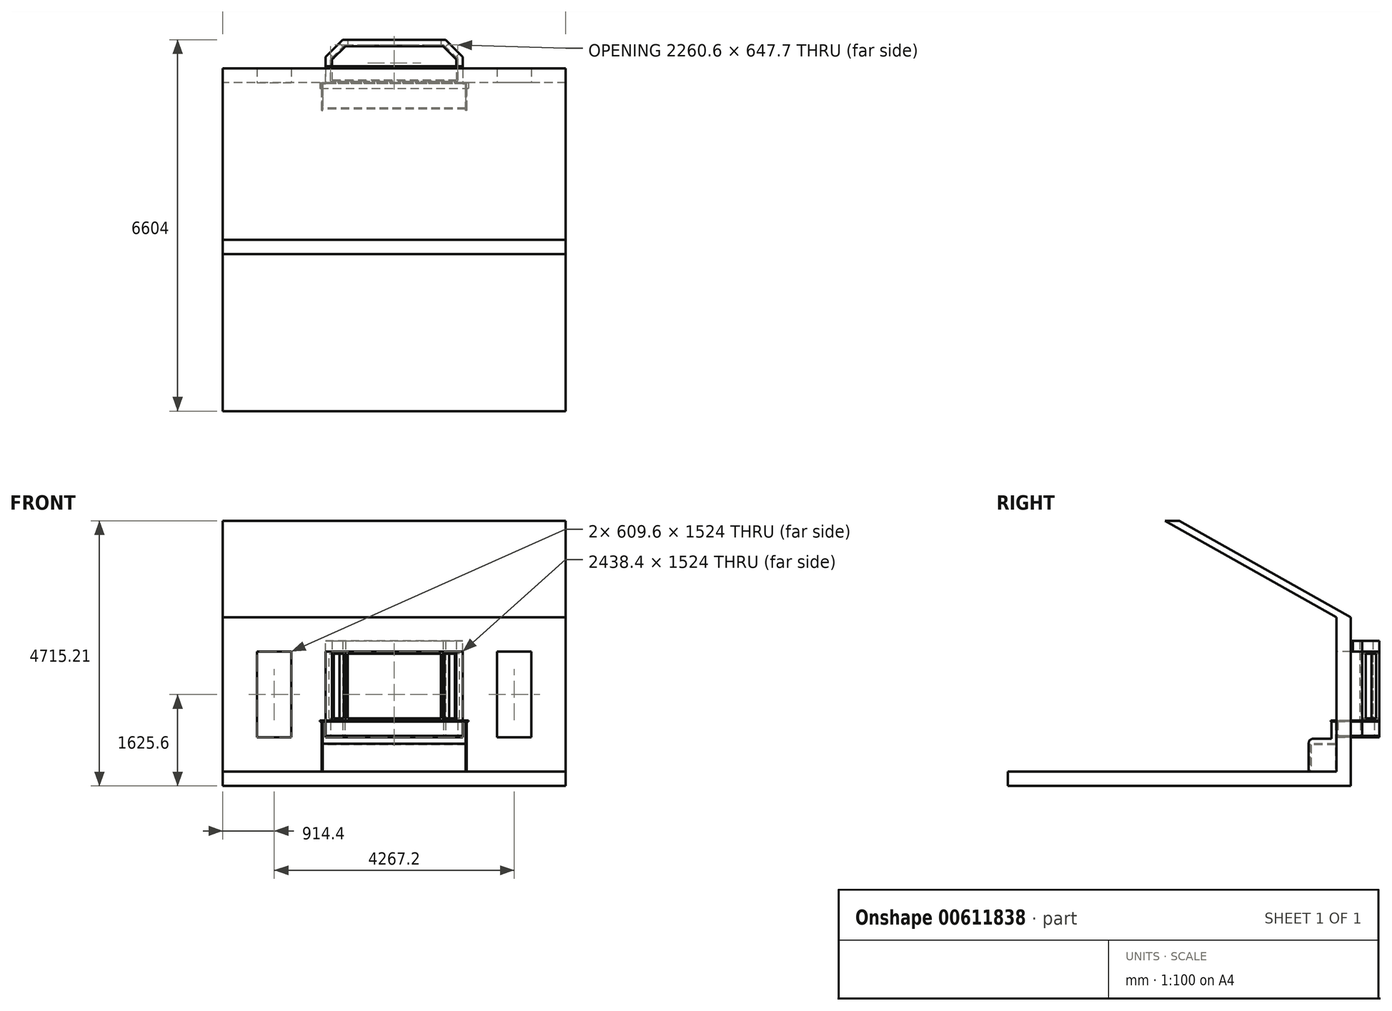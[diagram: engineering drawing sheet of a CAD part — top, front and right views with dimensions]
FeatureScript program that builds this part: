
annotation { "Feature Type Name" : "Feature", "Feature Type Description" : "" }
export const myFeature = defineFeature(function(context is Context, id is Id, definition is map)
    precondition{}
    {
        {
            var Q0;
            Q0=qCreatedBy(makeId("Top.planeOp"),FACE);
            var sketch = newSketch(context, id + "F0", { "sketchPlane" : qUnion([Q0])});
            skLineSegment(sketch, "E0.bottom", {"start": v(-3048, -3048) * mm, "end": v(3048, -3048) * mm});
            skLineSegment(sketch, "E0.top", {"start": v(-3048, 3048) * mm, "end": v(3048, 3048) * mm});
            skLineSegment(sketch, "E0.left", {"start": v(-3048, -3048) * mm, "end": v(-3048, 3048) * mm});
            skLineSegment(sketch, "E0.right", {"start": v(3048, -3048) * mm, "end": v(3048, 3048) * mm});
            skPoint(sketch, "E0.middle", {"position": v(0, 0) * mm});
            skSolve(sketch);
        }
        {
            var Q0;
            Q0=makeQuery(id+"F0.imprint","IMPRINT",FACE,{"disambiguationData":[TD([[makeQuery(id+"F0.imprint","IMPRINT",EDGE,{"derivedFrom":sQuery(id+"F0.wireOp",EDGE,"E0.bottom")}),1.0]])]});
            extrude(context, id + "F1", {"entities" : qUnion([Q0]), "oppositeDirection" : true, "depth" : 254 * mm, "offsetDistance" : 25.4 * mm});
        }
        {
            var Q0;
            Q0=makeQuery(id+"F1.opExtrude","CAP_FACE",FACE,{"disambiguationData":[OSD([sQuery(id+"F0.wireOp",EDGE,"E0.bottom"),sQuery(id+"F0.wireOp",EDGE,"E0.top"),sQuery(id+"F0.wireOp",EDGE,"E0.left"),sQuery(id+"F0.wireOp",EDGE,"E0.right")])],"isStart":true});
            var sketch = newSketch(context, id + "F2", { "sketchPlane" : qUnion([Q0])});
            skLineSegment(sketch, "E1.bottom", {"start": v(3048, 3048) * mm, "end": v(-3048, 3048) * mm});
            skLineSegment(sketch, "E1.top", {"start": v(3048, 2794) * mm, "end": v(-3048, 2794) * mm});
            skLineSegment(sketch, "E1.left", {"start": v(3048, 3048) * mm, "end": v(3048, 2794) * mm});
            skLineSegment(sketch, "E1.right", {"start": v(-3048, 3048) * mm, "end": v(-3048, 2794) * mm});
            skSolve(sketch);
        }
        {
            var Q0;
            Q0=makeQuery(id+"F2.imprint","IMPRINT",FACE,{"disambiguationData":[TD([[makeQuery(id+"F2.imprint","IMPRINT",EDGE,{"derivedFrom":sQuery(id+"F2.wireOp",EDGE,"E1.bottom")}),-1.0]])]});
            extrude(context, id + "F3", {"entities" : qUnion([Q0]), "operationType" : NewBodyOperationType.ADD, "depth" : 2743.2 * mm, "offsetDistance" : 25.4 * mm});
        }
        {
            var Q0;
            Q0=makeQuery(id+"F3.boolean.opBoolean","MERGE",FACE,{"derivedFrom":[makeQuery(id+"F1.opExtrude","SWEPT_FACE",FACE,{"disambiguationData":[OSD([sQuery(id+"F0.wireOp",EDGE,"E0.right")])]}),makeQuery(id+"F3.opExtrude","SWEPT_FACE",FACE,{"disambiguationData":[OSD([sQuery(id+"F2.wireOp",EDGE,"E1.left")])]})]});
            var sketch = newSketch(context, id + "F4", { "sketchPlane" : qUnion([Q0])});
            skLineSegment(sketch, "E2", {"start": v(3048, 2743.2) * mm, "end": v(0, 4461.21) * mm});
            skLineSegment(sketch, "E3", {"start": v(0, 4461.21) * mm, "end": v(-254, 4461.21) * mm});
            skLineSegment(sketch, "E4", {"start": v(-254, 4461.21) * mm, "end": v(2794, 2743.2) * mm});
            skLineSegment(sketch, "E5", {"start": v(2794, 2743.2) * mm, "end": v(3048, 2743.2) * mm});
            skSolve(sketch);
        }
        {
            var Q0;
            Q0=makeQuery(id+"F4.imprint","IMPRINT",FACE,{"disambiguationData":[TD([[makeQuery(id+"F4.imprint","IMPRINT",EDGE,{"derivedFrom":sQuery(id+"F4.wireOp",EDGE,"E2")}),1.0]])]});
            extrude(context, id + "F5", {"entities" : qUnion([Q0]), "operationType" : NewBodyOperationType.ADD, "oppositeDirection" : true, "depth" : 6096 * mm, "offsetDistance" : 25.4 * mm});
        }
        {
            var Q0;
            Q0=makeQuery(id+"F3.opExtrude","SWEPT_FACE",FACE,{"disambiguationData":[OSD([sQuery(id+"F2.wireOp",EDGE,"E1.top")])]});
            var sketch = newSketch(context, id + "F6", { "sketchPlane" : qUnion([Q0])});
            skLineSegment(sketch, "E6", {"start": v(0, 0) * mm, "end": v(0, 2743.2) * mm, "construction": true});
            skLineSegment(sketch, "E7", {"start": v(-3048, 1371.6) * mm, "end": v(3048, 1371.6) * mm, "construction": true});
            skLineSegment(sketch, "E8.bottom", {"start": v(-2438.4, 2133.6) * mm, "end": v(-1828.8, 2133.6) * mm});
            skLineSegment(sketch, "E8.top", {"start": v(-2438.4, 609.6) * mm, "end": v(-1828.8, 609.6) * mm});
            skLineSegment(sketch, "E8.left", {"start": v(-2438.4, 2133.6) * mm, "end": v(-2438.4, 609.6) * mm});
            skLineSegment(sketch, "E8.right", {"start": v(-1828.8, 2133.6) * mm, "end": v(-1828.8, 609.6) * mm});
            skPoint(sketch, "E8.middle", {"position": v(-2133.6, 1371.6) * mm});
            skLineSegment(sketch, "E9.MirrorCS", {"start": v(1828.8, 2133.6) * mm, "end": v(1828.8, 609.6) * mm});
            skLineSegment(sketch, "E10.MirrorCS", {"start": v(2438.4, 2133.6) * mm, "end": v(1828.8, 2133.6) * mm});
            skLineSegment(sketch, "E11.MirrorCS", {"start": v(2438.4, 2133.6) * mm, "end": v(2438.4, 609.6) * mm});
            skLineSegment(sketch, "E12.MirrorCS", {"start": v(2438.4, 609.6) * mm, "end": v(1828.8, 609.6) * mm});
            skSolve(sketch);
        }
        {
            var Q0;
            Q0=makeQuery(id+"F6.imprint","IMPRINT",FACE,{"disambiguationData":[TD([[makeQuery(id+"F6.imprint","IMPRINT",EDGE,{"derivedFrom":sQuery(id+"F6.wireOp",EDGE,"E8.bottom")}),-1.0]])]});
            var Q1;
            Q1=makeQuery(id+"F6.imprint","IMPRINT",FACE,{"disambiguationData":[TD([[makeQuery(id+"F6.imprint","IMPRINT",EDGE,{"derivedFrom":sQuery(id+"F6.wireOp",EDGE,"E9.MirrorCS")}),1.0]])]});
            extrude(context, id + "F7", {"entities" : qUnion([Q0, Q1]), "operationType" : NewBodyOperationType.REMOVE, "oppositeDirection" : true, "depth" : 304.8 * mm, "offsetDistance" : 25.4 * mm});
        }
        {
            var Q0;
            Q0=makeQuery(id+"F3.opExtrude","SWEPT_FACE",FACE,{"disambiguationData":[OSD([sQuery(id+"F2.wireOp",EDGE,"E1.top")])]});
            var sketch = newSketch(context, id + "F8", { "sketchPlane" : qUnion([Q0])});
            skLineSegment(sketch, "E13", {"start": v(0, 2743.2) * mm, "end": v(0, 0) * mm, "construction": true});
            skLineSegment(sketch, "E14", {"start": v(3048, 1371.6) * mm, "end": v(-3048, 1371.6) * mm, "construction": true});
            skLineSegment(sketch, "E15.bottom", {"start": v(1219.2, 2133.6) * mm, "end": v(-1219.2, 2133.6) * mm});
            skLineSegment(sketch, "E15.top", {"start": v(1219.2, 609.6) * mm, "end": v(-1219.2, 609.6) * mm});
            skLineSegment(sketch, "E15.left", {"start": v(1219.2, 2133.6) * mm, "end": v(1219.2, 609.6) * mm});
            skLineSegment(sketch, "E15.right", {"start": v(-1219.2, 2133.6) * mm, "end": v(-1219.2, 609.6) * mm});
            skPoint(sketch, "E15.middle", {"position": v(0, 1371.6) * mm});
            skSolve(sketch);
        }
        {
            var Q0;
            Q0 = qSketchRegion(id + "F8", true);
            extrude(context, id + "F9", {"entities" : qUnion([Q0]), "operationType" : NewBodyOperationType.REMOVE, "oppositeDirection" : true, "depth" : 304.8 * mm, "offsetDistance" : 25.4 * mm});
        }
        {
            var Q0;
            Q0=makeQuery(id+"F9.boolean.opBoolean","COPY",FACE,{"derivedFrom":makeQuery(id+"F9.opExtrude","SWEPT_FACE",FACE,{"disambiguationData":[OSD([sQuery(id+"F8.wireOp",EDGE,"E15.top")])]})});
            var sketch = newSketch(context, id + "F10", { "sketchPlane" : qUnion([Q0])});
            skLineSegment(sketch, "E16", {"start": v(-1219.2, 2794) * mm, "end": v(-1219.2, 3251.2) * mm});
            skLineSegment(sketch, "E17", {"start": v(-1219.2, 3251.2) * mm, "end": v(-914.4, 3556) * mm});
            skLineSegment(sketch, "E18", {"start": v(914.4, 3556) * mm, "end": v(1219.2, 3251.2) * mm});
            skLineSegment(sketch, "E19", {"start": v(1219.2, 3251.2) * mm, "end": v(1219.2, 2794) * mm});
            skLineSegment(sketch, "E20", {"start": v(1219.2, 2794) * mm, "end": v(0, 2794) * mm});
            skLineSegment(sketch, "E21", {"start": v(0, 2794) * mm, "end": v(-1219.2, 2794) * mm});
            skLineSegment(sketch, "E22", {"start": v(-914.4, 3556) * mm, "end": v(914.4, 3556) * mm});
            skSolve(sketch);
        }
        {
            var Q0;
            {var subQ1=sQuery(id+"F10.wireOp",EDGE,"E17");Q0=makeQuery(id+"F10.imprint","IMPRINT",FACE,{"disambiguationData":[TD([[makeQuery(id+"F10.imprint","IMPRINT",EDGE,{"derivedFrom":subQ1}),-1.0]])]});}
            var Q1;
            {var subQ1=sQuery(id+"F10.wireOp",EDGE,"E20");Q1=makeQuery(id+"F10.imprint","IMPRINT",FACE,{"disambiguationData":[TD([[makeQuery(id+"F10.imprint","IMPRINT",EDGE,{"derivedFrom":subQ1}),-1.0]])]});}
            extrude(context, id + "F11", {"entities" : qUnion([Q0, Q1]), "depth" : 25.4 * mm, "offsetDistance" : 25.4 * mm});
        }
        {
            var Q0;
            Q0=makeQuery(id+"F11.opExtrude","CAP_FACE",FACE,{"disambiguationData":[OSD([sQuery(id+"F10.wireOp",EDGE,"E16"),sQuery(id+"F10.wireOp",EDGE,"E17"),sQuery(id+"F10.wireOp",EDGE,"E18"),sQuery(id+"F10.wireOp",EDGE,"E19"),sQuery(id+"F10.wireOp",EDGE,"E20"),sQuery(id+"F10.wireOp",EDGE,"E21"),sQuery(id+"F10.wireOp",EDGE,"E22")])],"isStart":false});
            var sketch = newSketch(context, id + "F12", { "sketchPlane" : qUnion([Q0])});
            skLineSegment(sketch, "E23.0", {"start": v(-1219.2, 2794) * mm, "end": v(-1219.2, 3251.2) * mm});
            skLineSegment(sketch, "E24.0", {"start": v(-1219.2, 3251.2) * mm, "end": v(-914.4, 3556) * mm});
            skLineSegment(sketch, "E25.0", {"start": v(-914.4, 3556) * mm, "end": v(914.4, 3556) * mm});
            skLineSegment(sketch, "E26.0", {"start": v(914.4, 3556) * mm, "end": v(1219.2, 3251.2) * mm});
            skLineSegment(sketch, "E27.0", {"start": v(1219.2, 3251.2) * mm, "end": v(1219.2, 2794) * mm});
            skLineSegment(sketch, "E28.0", {"start": v(1219.2, 2794) * mm, "end": v(-1219.2, 2794) * mm});
            skLineSegment(sketch, "E29", {"start": v(-877.58, 3467.1) * mm, "end": v(877.58, 3467.1) * mm});
            skLineSegment(sketch, "E30", {"start": v(877.58, 3467.1) * mm, "end": v(1130.3, 3214.38) * mm});
            skLineSegment(sketch, "E31", {"start": v(1130.3, 3214.38) * mm, "end": v(1130.3, 2819.4) * mm});
            skLineSegment(sketch, "E32", {"start": v(1130.3, 2819.4) * mm, "end": v(-1130.3, 2819.4) * mm});
            skLineSegment(sketch, "E33", {"start": v(-1130.3, 2819.4) * mm, "end": v(-1130.3, 3214.38) * mm});
            skLineSegment(sketch, "E34", {"start": v(-1130.3, 3214.38) * mm, "end": v(-877.58, 3467.1) * mm});
            skLineSegment(sketch, "E35", {"start": v(-1130.3, 3149.6) * mm, "end": v(1130.3, 3149.6) * mm});
            skLineSegment(sketch, "E36", {"start": v(1130.3, 3149.6) * mm, "end": v(1130.3, 3124.2) * mm});
            skLineSegment(sketch, "E37", {"start": v(1130.3, 3124.2) * mm, "end": v(-1130.3, 3124.2) * mm});
            skLineSegment(sketch, "E38", {"start": v(-1130.3, 3124.2) * mm, "end": v(-1130.3, 3149.6) * mm});
            skSolve(sketch);
        }
        {
            var Q0;
            Q0=makeQuery(id+"F12.imprint","IMPRINT",FACE,{"disambiguationData":[TD([[makeQuery(id+"F12.imprint","IMPRINT",EDGE,{"derivedFrom":sQuery(id+"F12.wireOp",EDGE,"E23.0")}),-1.0]])]});
            extrude(context, id + "F13", {"entities" : qUnion([Q0]), "depth" : 254 * mm, "offsetDistance" : 25.4 * mm});
        }
        {
            var Q0;
            Q0=makeQuery(id+"F13.opExtrude","CAP_FACE",FACE,{"disambiguationData":[OSD([sQuery(id+"F12.wireOp",EDGE,"E23.0"),sQuery(id+"F12.wireOp",EDGE,"E24.0"),sQuery(id+"F12.wireOp",EDGE,"E25.0"),sQuery(id+"F12.wireOp",EDGE,"E26.0"),sQuery(id+"F12.wireOp",EDGE,"E27.0"),sQuery(id+"F12.wireOp",EDGE,"E28.0"),sQuery(id+"F12.wireOp",EDGE,"E29"),sQuery(id+"F12.wireOp",EDGE,"E30"),sQuery(id+"F12.wireOp",EDGE,"E31"),sQuery(id+"F12.wireOp",EDGE,"E32"),sQuery(id+"F12.wireOp",EDGE,"E33"),sQuery(id+"F12.wireOp",EDGE,"E34"),sQuery(id+"F12.wireOp",EDGE,"E35"),sQuery(id+"F12.wireOp",EDGE,"E37")])],"isStart":false});
            var sketch = newSketch(context, id + "F14", { "sketchPlane" : qUnion([Q0])});
            skLineSegment(sketch, "E39.0.0", {"start": v(1219.2, 2794) * mm, "end": v(1219.2, 3251.2) * mm});
            skLineSegment(sketch, "E39.0.1", {"start": v(1219.2, 3251.2) * mm, "end": v(914.4, 3556) * mm});
            skLineSegment(sketch, "E39.0.2", {"start": v(914.4, 3556) * mm, "end": v(-914.4, 3556) * mm});
            skLineSegment(sketch, "E39.0.3", {"start": v(-914.4, 3556) * mm, "end": v(-1219.2, 3251.2) * mm});
            skLineSegment(sketch, "E39.0.4", {"start": v(-1219.2, 3251.2) * mm, "end": v(-1219.2, 2794) * mm});
            skLineSegment(sketch, "E39.0.5", {"start": v(-1219.2, 2794) * mm, "end": v(1219.2, 2794) * mm});
            skLineSegment(sketch, "E40.bottom", {"start": v(-1320.8, 2794) * mm, "end": v(1320.8, 2794) * mm});
            skLineSegment(sketch, "E40.top", {"start": v(-1320.8, 2692.4) * mm, "end": v(1320.8, 2692.4) * mm});
            skLineSegment(sketch, "E40.left", {"start": v(-1320.8, 2794) * mm, "end": v(-1320.8, 2692.4) * mm});
            skLineSegment(sketch, "E40.right", {"start": v(1320.8, 2794) * mm, "end": v(1320.8, 2692.4) * mm});
            skLineSegment(sketch, "E41.bottom", {"start": v(-1104.9, 3203.86) * mm, "end": v(-867.06, 3441.7) * mm});
            skLineSegment(sketch, "E41.top", {"start": v(-1104.9, 2844.8) * mm, "end": v(1104.9, 2844.8) * mm});
            skLineSegment(sketch, "E41.left", {"start": v(-1104.9, 3203.86) * mm, "end": v(-1104.9, 2844.8) * mm});
            skLineSegment(sketch, "E41.right", {"start": v(1104.9, 3203.86) * mm, "end": v(1104.9, 2844.8) * mm});
            skLineSegment(sketch, "E42", {"start": v(-867.06, 3441.7) * mm, "end": v(867.06, 3441.7) * mm});
            skLineSegment(sketch, "E43", {"start": v(867.06, 3441.7) * mm, "end": v(1104.9, 3203.86) * mm});
            skSolve(sketch);
        }
        {
            var Q0;
            Q0 = qSketchRegion(id + "F14", true);
            extrude(context, id + "F15", {"entities" : qUnion([Q0]), "depth" : 19.05 * mm, "offsetDistance" : 25.4 * mm});
        }
        {
            var Q0;
            Q0=makeQuery(id+"F3.boolean.opBoolean","MERGE",FACE,{"derivedFrom":[makeQuery(id+"F1.opExtrude","SWEPT_FACE",FACE,{"disambiguationData":[OSD([sQuery(id+"F0.wireOp",EDGE,"E0.top")])]}),makeQuery(id+"F3.opExtrude","SWEPT_FACE",FACE,{"disambiguationData":[OSD([sQuery(id+"F2.wireOp",EDGE,"E1.bottom")])]})]});
            var sketch = newSketch(context, id + "F16", { "sketchPlane" : qUnion([Q0])});
            skLineSegment(sketch, "E44.bottom", {"start": v(-1219.2, 2133.6) * mm, "end": v(1219.2, 2133.6) * mm});
            skLineSegment(sketch, "E44.top", {"start": v(-1219.2, 2324.1) * mm, "end": v(1219.2, 2324.1) * mm});
            skLineSegment(sketch, "E44.left", {"start": v(-1219.2, 2133.6) * mm, "end": v(-1219.2, 2324.1) * mm});
            skLineSegment(sketch, "E44.right", {"start": v(1219.2, 2133.6) * mm, "end": v(1219.2, 2324.1) * mm});
            skSolve(sketch);
        }
        {
            var Q0;
            Q0 = qSketchRegion(id + "F16", true);
            extrude(context, id + "F17", {"entities" : qUnion([Q0]), "depth" : 38.1 * mm, "offsetDistance" : 25.4 * mm});
        }
        {
            var Q0;
            Q0=makeQuery(id+"F3.opExtrude","SWEPT_FACE",FACE,{"disambiguationData":[OSD([sQuery(id+"F2.wireOp",EDGE,"E1.top")])]});
            var sketch = newSketch(context, id + "F18", { "sketchPlane" : qUnion([Q0])});
            skLineSegment(sketch, "E45.0", {"start": v(-1320.8, 889) * mm, "end": v(1320.8, 889) * mm});
            skLineSegment(sketch, "E46.bottom", {"start": v(-1270, 889) * mm, "end": v(1270, 889) * mm});
            skLineSegment(sketch, "E46.top", {"start": v(-1270, 0) * mm, "end": v(1270, 0) * mm});
            skLineSegment(sketch, "E46.left", {"start": v(-1270, 889) * mm, "end": v(-1270, 0) * mm});
            skLineSegment(sketch, "E46.right", {"start": v(1270, 889) * mm, "end": v(1270, 0) * mm});
            skSolve(sketch);
        }
        {
            var Q0;
            {var subQ5=makeQuery(id+"F9.boolean.opBoolean","COPY",EDGE,{"derivedFrom":makeQuery(id+"F9.opExtrude","CAP_EDGE",EDGE,{"disambiguationData":[OSD([sQuery(id+"F8.wireOp",EDGE,"E15.top")])],"isStart":true})});Q0=makeQuery(id+"F18.imprint","IMPRINT",FACE,{"disambiguationData":[TD([[makeQuery(id+"F18.imprint","IMPRINT",EDGE,{"derivedFrom":subQ5}),-1.0]])]});}
            var Q1;
            Q1=makeQuery(id+"F18.imprint","IMPRINT",FACE,{"disambiguationData":[TD([[makeQuery(id+"F18.imprint","IMPRINT",EDGE,{"derivedFrom":sQuery(id+"F18.wireOp",EDGE,"E46.top")}),-1.0]])]});
            extrude(context, id + "F19", {"entities" : qUnion([Q0, Q1]), "depth" : 19.05 * mm, "offsetDistance" : 25.4 * mm});
        }
        {
            var Q0;
            Q0=makeQuery(id+"F19.opExtrude","SWEPT_FACE",FACE,{"disambiguationData":[OSD([sQuery(id+"F18.wireOp",EDGE,"E46.left")])]});
            var sketch = newSketch(context, id + "F20", { "sketchPlane" : qUnion([Q0])});
            skLineSegment(sketch, "E47.bottom", {"start": v(-2794, 889) * mm, "end": v(-2705.1, 889) * mm});
            skLineSegment(sketch, "E47.top", {"start": v(-2794, 0) * mm, "end": v(-2705.1, 0) * mm});
            skLineSegment(sketch, "E47.left", {"start": v(-2794, 889) * mm, "end": v(-2794, 0) * mm});
            skLineSegment(sketch, "E47.right", {"start": v(-2705.1, 889) * mm, "end": v(-2705.1, 0) * mm});
            skLineSegment(sketch, "E48.bottom", {"start": v(-2705.1, 0) * mm, "end": v(-2298.7, 0) * mm});
            skLineSegment(sketch, "E48.top", {"start": v(-2705.1, 584.2) * mm, "end": v(-2298.7, 584.2) * mm});
            skLineSegment(sketch, "E48.left", {"start": v(-2705.1, 0) * mm, "end": v(-2705.1, 584.2) * mm});
            skLineSegment(sketch, "E48.right", {"start": v(-2298.7, 0) * mm, "end": v(-2298.7, 584.2) * mm});
            skSolve(sketch);
        }
        {
            var Q0;
            {var subQ0=sQuery(id+"F20.wireOp",EDGE,"E47.left");Q0=makeQuery(id+"F20.imprint","IMPRINT",FACE,{"disambiguationData":[TD([[makeQuery(id+"F20.imprint","IMPRINT",EDGE,{"derivedFrom":subQ0}),1.0]])]});}
            var Q1;
            Q1=makeQuery(id+"F20.imprint","IMPRINT",FACE,{"disambiguationData":[TD([[makeQuery(id+"F20.imprint","IMPRINT",EDGE,{"derivedFrom":sQuery(id+"F20.wireOp",EDGE,"E48.bottom")}),1.0]])]});
            var Q2;
            {var subQ3=sQuery(id+"F20.wireOp",EDGE,"E47.right");Q2=makeQuery(id+"F20.imprint","IMPRINT",FACE,{"disambiguationData":[TD([[makeQuery(id+"F20.imprint","IMPRINT",EDGE,{"derivedFrom":subQ3}),-1.0]])]});}
            extrude(context, id + "F21", {"entities" : qUnion([Q0, Q1, Q2]), "depth" : 19.05 * mm, "offsetDistance" : 25.4 * mm});
        }
        {
            var Q0;
            Q0=makeQuery(id+"F19.opExtrude","SWEPT_FACE",FACE,{"disambiguationData":[OSD([sQuery(id+"F18.wireOp",EDGE,"E46.right")])]});
            var sketch = newSketch(context, id + "F22", { "sketchPlane" : qUnion([Q0])});
            skLineSegment(sketch, "E49.bottom", {"start": v(2794, 889) * mm, "end": v(2705.1, 889) * mm});
            skLineSegment(sketch, "E49.top", {"start": v(2794, 0) * mm, "end": v(2705.1, 0) * mm});
            skLineSegment(sketch, "E49.left", {"start": v(2794, 889) * mm, "end": v(2794, 0) * mm});
            skLineSegment(sketch, "E49.right", {"start": v(2705.1, 889) * mm, "end": v(2705.1, 0) * mm});
            skLineSegment(sketch, "E50.bottom", {"start": v(2705.1, 0) * mm, "end": v(2298.7, 0) * mm});
            skLineSegment(sketch, "E50.top", {"start": v(2705.1, 584.2) * mm, "end": v(2298.7, 584.2) * mm});
            skLineSegment(sketch, "E50.left", {"start": v(2705.1, 0) * mm, "end": v(2705.1, 584.2) * mm});
            skLineSegment(sketch, "E50.right", {"start": v(2298.7, 0) * mm, "end": v(2298.7, 584.2) * mm});
            skSolve(sketch);
        }
        {
            var Q0;
            Q0 = qSketchRegion(id + "F22", true);
            extrude(context, id + "F23", {"entities" : qUnion([Q0]), "depth" : 19.05 * mm, "offsetDistance" : 25.4 * mm});
        }
        {
            var Q0;
            Q0=makeQuery(id+"F21.opExtrude","CAP_FACE",FACE,{"disambiguationData":[OSD([sQuery(id+"F20.wireOp",EDGE,"E47.bottom"),sQuery(id+"F20.wireOp",EDGE,"E47.top"),sQuery(id+"F20.wireOp",EDGE,"E47.left"),sQuery(id+"F20.wireOp",EDGE,"E47.right"),sQuery(id+"F20.wireOp",EDGE,"E48.bottom"),sQuery(id+"F20.wireOp",EDGE,"E48.top"),sQuery(id+"F20.wireOp",EDGE,"E48.right")])],"isStart":true});
            var sketch = newSketch(context, id + "F24", { "sketchPlane" : qUnion([Q0])});
            skLineSegment(sketch, "E51.0", {"start": v(2774.95, 889) * mm, "end": v(2774.95, 0) * mm});
            skLineSegment(sketch, "E52.bottom", {"start": v(2774.95, 495.3) * mm, "end": v(2324.1, 495.3) * mm});
            skLineSegment(sketch, "E52.top", {"start": v(2774.95, 476.25) * mm, "end": v(2324.1, 476.25) * mm});
            skLineSegment(sketch, "E52.left", {"start": v(2774.95, 495.3) * mm, "end": v(2774.95, 476.25) * mm});
            skLineSegment(sketch, "E52.right", {"start": v(2324.1, 495.3) * mm, "end": v(2324.1, 476.25) * mm});
            skLineSegment(sketch, "E53.bottom", {"start": v(2324.1, 476.25) * mm, "end": v(2343.15, 476.25) * mm});
            skLineSegment(sketch, "E53.top", {"start": v(2324.1, 0) * mm, "end": v(2343.15, 0) * mm});
            skLineSegment(sketch, "E53.left", {"start": v(2324.1, 476.25) * mm, "end": v(2324.1, 0) * mm});
            skLineSegment(sketch, "E53.right", {"start": v(2343.15, 476.25) * mm, "end": v(2343.15, 0) * mm});
            skSolve(sketch);
        }
        {
            var Q0;
            Q0 = qSketchRegion(id + "F24", true);
            extrude(context, id + "F25", {"entities" : qUnion([Q0]), "endBound" : BoundingType.UP_TO_NEXT, "depth" : 25.4 * mm, "offsetDistance" : 25.4 * mm});
        }
        {
            var Q0;
            Q0=makeQuery(id+"F23.opExtrude","SWEPT_EDGE",EDGE,{"disambiguationData":[OSD([sQuery(id+"F22.wireOp",EDGE,"E50.top"),sQuery(id+"F22.wireOp",EDGE,"E50.right")])]});
            var Q1;
            Q1=makeQuery(id+"F21.opExtrude","SWEPT_EDGE",EDGE,{"disambiguationData":[OSD([sQuery(id+"F20.wireOp",EDGE,"E48.top"),sQuery(id+"F20.wireOp",EDGE,"E48.right")])]});
            fillet(context, id + "F26", {"entities" : qUnion([Q0, Q1]), "radius" : 76.2 * mm, "tangentPropagation" : true, "allowEdgeOverflow" : false});
        }
        {
            var Q0;
            Q0=makeQuery(id+"F15.opExtrude","CAP_FACE",FACE,{"disambiguationData":[OSD([sQuery(id+"F14.wireOp",EDGE,"E39.0.0"),sQuery(id+"F14.wireOp",EDGE,"E39.0.1"),sQuery(id+"F14.wireOp",EDGE,"E39.0.2"),sQuery(id+"F14.wireOp",EDGE,"E39.0.3"),sQuery(id+"F14.wireOp",EDGE,"E39.0.4"),sQuery(id+"F14.wireOp",EDGE,"E40.bottom"),sQuery(id+"F14.wireOp",EDGE,"E40.top"),sQuery(id+"F14.wireOp",EDGE,"E40.left"),sQuery(id+"F14.wireOp",EDGE,"E40.right"),sQuery(id+"F14.wireOp",EDGE,"E41.bottom"),sQuery(id+"F14.wireOp",EDGE,"E41.top"),sQuery(id+"F14.wireOp",EDGE,"E41.left"),sQuery(id+"F14.wireOp",EDGE,"E41.right"),sQuery(id+"F14.wireOp",EDGE,"E42"),sQuery(id+"F14.wireOp",EDGE,"E43")])],"isStart":false});
            var sketch = newSketch(context, id + "F27", { "sketchPlane" : qUnion([Q0])});
            skLineSegment(sketch, "E54.0", {"start": v(-3048, 3048) * mm, "end": v(3048, 3048) * mm});
            skLineSegment(sketch, "E55", {"start": v(1219.2, 3048) * mm, "end": v(1219.2, 3251.2) * mm});
            skLineSegment(sketch, "E56", {"start": v(1219.2, 3251.2) * mm, "end": v(914.4, 3556) * mm});
            skLineSegment(sketch, "E57", {"start": v(914.4, 3556) * mm, "end": v(-914.4, 3556) * mm});
            skLineSegment(sketch, "E58", {"start": v(-914.4, 3556) * mm, "end": v(-1219.2, 3251.2) * mm});
            skLineSegment(sketch, "E59", {"start": v(-1219.2, 3251.2) * mm, "end": v(-1219.2, 3048) * mm});
            skLineSegment(sketch, "E60", {"start": v(-1219.2, 3048) * mm, "end": v(-1104.9, 3048) * mm});
            skLineSegment(sketch, "E61", {"start": v(-1104.9, 3048) * mm, "end": v(-1104.9, 3203.86) * mm});
            skLineSegment(sketch, "E62", {"start": v(-1104.9, 3203.86) * mm, "end": v(-867.06, 3441.7) * mm});
            skLineSegment(sketch, "E63", {"start": v(-867.06, 3441.7) * mm, "end": v(867.06, 3441.7) * mm});
            skLineSegment(sketch, "E64", {"start": v(867.06, 3441.7) * mm, "end": v(1104.9, 3203.86) * mm});
            skLineSegment(sketch, "E65", {"start": v(1104.9, 3203.86) * mm, "end": v(1104.9, 3048) * mm});
            skLineSegment(sketch, "E66", {"start": v(1104.9, 3048) * mm, "end": v(1219.2, 3048) * mm});
            skSolve(sketch);
        }
        {
            var Q0;
            Q0=makeQuery(id+"F27.imprint","IMPRINT",FACE,{"disambiguationData":[TD([[makeQuery(id+"F27.imprint","IMPRINT",EDGE,{"derivedFrom":sQuery(id+"F27.wireOp",EDGE,"E55")}),-1.0]])]});
            var Q1;
            Q1=makeQuery(id+"F17.opExtrude","SWEPT_FACE",FACE,{"disambiguationData":[OSD([sQuery(id+"F16.wireOp",EDGE,"E44.bottom")])]});
            extrude(context, id + "F28", {"entities" : qUnion([Q0]), "endBound" : BoundingType.UP_TO_SURFACE, "depth" : 25.4 * mm, "endBoundEntityFace" : qUnion([Q1]), "offsetDistance" : 25.4 * mm});
        }
        {
            var Q0;
            Q0=makeQuery(id+"F28.opExtrude","SWEPT_FACE",FACE,{"disambiguationData":[OSD([sQuery(id+"F27.wireOp",EDGE,"E63")])]});
            var sketch = newSketch(context, id + "F29", { "sketchPlane" : qUnion([Q0])});
            skLineSegment(sketch, "E67.bottom", {"start": v(-828.96, 2095.5) * mm, "end": v(828.96, 2095.5) * mm});
            skLineSegment(sketch, "E67.top", {"start": v(-828.96, 946.15) * mm, "end": v(828.96, 946.15) * mm});
            skLineSegment(sketch, "E67.left", {"start": v(-828.96, 2095.5) * mm, "end": v(-828.96, 946.15) * mm});
            skLineSegment(sketch, "E67.right", {"start": v(828.96, 2095.5) * mm, "end": v(828.96, 946.15) * mm});
            skSolve(sketch);
        }
        {
            var Q0;
            Q0 = qSketchRegion(id + "F29", true);
            extrude(context, id + "F30", {"entities" : qUnion([Q0]), "operationType" : NewBodyOperationType.REMOVE, "oppositeDirection" : true, "depth" : 127 * mm, "offsetDistance" : 25.4 * mm});
        }
        {
            var Q0;
            Q0=makeQuery(id+"F28.opExtrude","SWEPT_FACE",FACE,{"disambiguationData":[OSD([sQuery(id+"F27.wireOp",EDGE,"E62")])]});
            var sketch = newSketch(context, id + "F31", { "sketchPlane" : qUnion([Q0])});
            skLineSegment(sketch, "E68.bottom", {"start": v(1522.29, 2095.5) * mm, "end": v(1782.45, 2095.5) * mm});
            skLineSegment(sketch, "E68.top", {"start": v(1522.29, 946.15) * mm, "end": v(1782.45, 946.15) * mm});
            skLineSegment(sketch, "E68.left", {"start": v(1522.29, 2095.5) * mm, "end": v(1522.29, 946.15) * mm});
            skLineSegment(sketch, "E68.right", {"start": v(1782.45, 2095.5) * mm, "end": v(1782.45, 946.15) * mm});
            skSolve(sketch);
        }
        {
            var Q0;
            Q0 = qSketchRegion(id + "F31", true);
            extrude(context, id + "F32", {"entities" : qUnion([Q0]), "operationType" : NewBodyOperationType.REMOVE, "oppositeDirection" : true, "depth" : 127 * mm, "offsetDistance" : 25.4 * mm});
        }
        {
            var Q0;
            Q0=makeQuery(id+"F28.opExtrude","SWEPT_FACE",FACE,{"disambiguationData":[OSD([sQuery(id+"F27.wireOp",EDGE,"E64")])]});
            var sketch = newSketch(context, id + "F33", { "sketchPlane" : qUnion([Q0])});
            skLineSegment(sketch, "E69.bottom", {"start": v(-1782.45, 2095.5) * mm, "end": v(-1522.29, 2095.5) * mm});
            skLineSegment(sketch, "E69.top", {"start": v(-1782.45, 946.15) * mm, "end": v(-1522.29, 946.15) * mm});
            skLineSegment(sketch, "E69.left", {"start": v(-1782.45, 2095.5) * mm, "end": v(-1782.45, 946.15) * mm});
            skLineSegment(sketch, "E69.right", {"start": v(-1522.29, 2095.5) * mm, "end": v(-1522.29, 946.15) * mm});
            skSolve(sketch);
        }
        {
            var Q0;
            Q0 = qSketchRegion(id + "F33", true);
            extrude(context, id + "F34", {"entities" : qUnion([Q0]), "operationType" : NewBodyOperationType.REMOVE, "oppositeDirection" : true, "depth" : 127 * mm, "offsetDistance" : 25.4 * mm});
        }
        {
            var Q0;
            Q0=makeQuery(id+"F28.opExtrude","CAP_FACE",FACE,{"disambiguationData":[OSD([sQuery(id+"F27.wireOp",EDGE,"E55"),sQuery(id+"F27.wireOp",EDGE,"E56"),sQuery(id+"F27.wireOp",EDGE,"E57"),sQuery(id+"F27.wireOp",EDGE,"E58"),sQuery(id+"F27.wireOp",EDGE,"E59"),sQuery(id+"F27.wireOp",EDGE,"E60"),sQuery(id+"F27.wireOp",EDGE,"E61"),sQuery(id+"F27.wireOp",EDGE,"E62"),sQuery(id+"F27.wireOp",EDGE,"E63"),sQuery(id+"F27.wireOp",EDGE,"E64"),sQuery(id+"F27.wireOp",EDGE,"E65"),sQuery(id+"F27.wireOp",EDGE,"E66")])],"isStart":false});
            var Q1;
            Q1=makeQuery(id+"F17.opExtrude","SWEPT_FACE",FACE,{"disambiguationData":[OSD([sQuery(id+"F16.wireOp",EDGE,"E44.top")])]});
            extrude(context, id + "F35", {"entities" : qUnion([Q0]), "endBound" : BoundingType.UP_TO_SURFACE, "depth" : 25.4 * mm, "endBoundEntityFace" : qUnion([Q1]), "offsetDistance" : 25.4 * mm});
        }
    });
